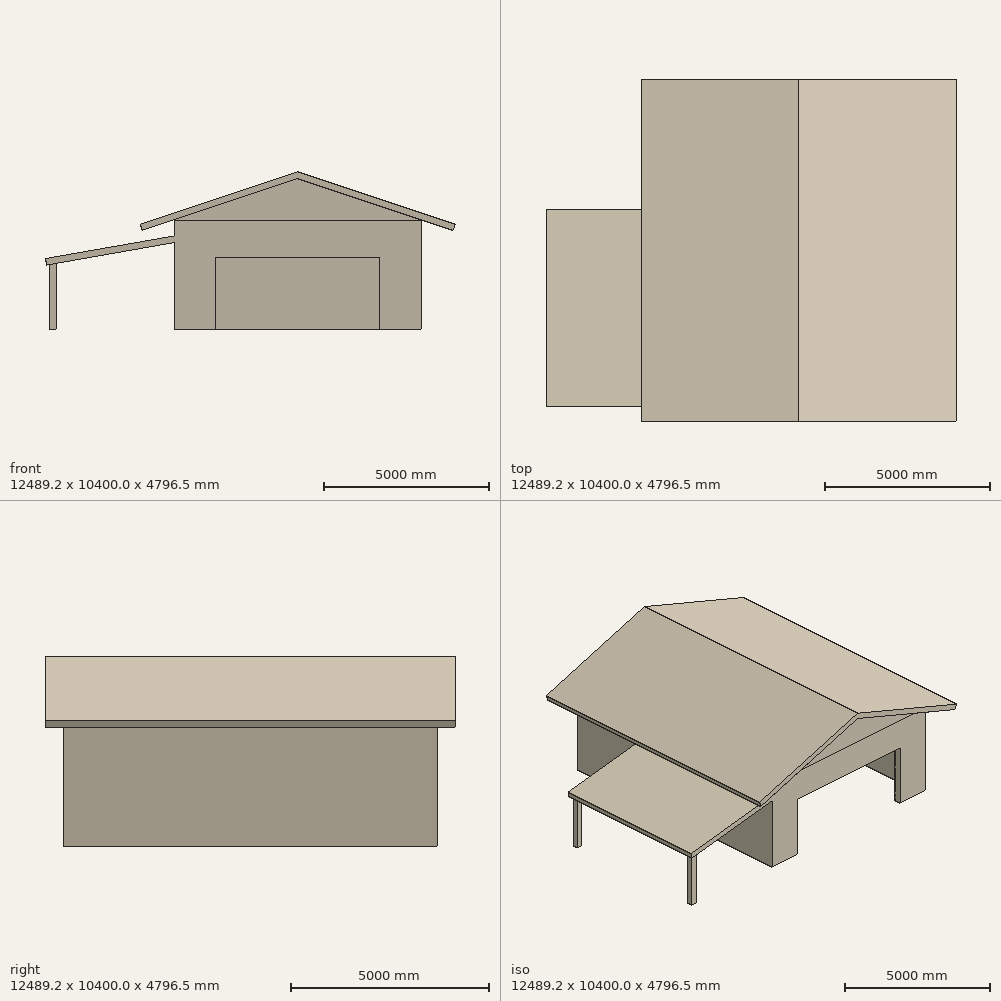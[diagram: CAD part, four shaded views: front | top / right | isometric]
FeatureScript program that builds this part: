
annotation { "Feature Type Name" : "Feature", "Feature Type Description" : "" }
export const myFeature = defineFeature(function(context is Context, id is Id, definition is map)
    precondition{}
    {
        {
            var Q0;
            Q0=qCreatedBy(makeId("Top.planeOp"),FACE);
            var sketch = newSketch(context, id + "F0", { "sketchPlane" : qUnion([Q0])});
            skLineSegment(sketch, "E0.bottom", {"start": v(-7500, 9500) * mm, "end": v(0, 9500) * mm});
            skLineSegment(sketch, "E0.top", {"start": v(-7500, 0) * mm, "end": v(0, 0) * mm});
            skLineSegment(sketch, "E0.left", {"start": v(-7500, 9500) * mm, "end": v(-7500, 0) * mm});
            skLineSegment(sketch, "E0.right", {"start": v(0, 9500) * mm, "end": v(0, 0) * mm});
            skLineSegment(sketch, "E1.bottom", {"start": v(-6186.75, 4848.57) * mm, "end": v(-4436.75, 4848.57) * mm, "construction": true});
            skLineSegment(sketch, "E1.top", {"start": v(-6186.75, 648.57) * mm, "end": v(-4436.75, 648.57) * mm, "construction": true});
            skLineSegment(sketch, "E1.left", {"start": v(-6186.75, 4848.57) * mm, "end": v(-6186.75, 648.57) * mm, "construction": true});
            skLineSegment(sketch, "E1.right", {"start": v(-4436.75, 4848.57) * mm, "end": v(-4436.75, 648.57) * mm, "construction": true});
            skLineSegment(sketch, "E2", {"start": v(0, 7250) * mm, "end": v(-7500, 7250) * mm, "construction": true});
            skSolve(sketch);
        }
        {
            var Q0;
            Q0=makeQuery(id+"F0.imprint","IMPRINT",FACE,{"disambiguationData":[TD([[makeQuery(id+"F0.imprint","IMPRINT",EDGE,{"derivedFrom":sQuery(id+"F0.wireOp",EDGE,"E0.bottom")}),-1.0]])]});
            extrude(context, id + "F1", {"entities" : qUnion([Q0]), "offsetDistance" : 25 * mm, "depth" : 3300 * mm});
        }
        {
            var Q0;
            Q0=makeQuery(id+"F1.opExtrude","SWEPT_FACE",FACE,{"disambiguationData":[OSD([sQuery(id+"F0.wireOp",EDGE,"E0.top")])]});
            var Q1;
            Q1=makeQuery(id+"F1.opExtrude","SWEPT_FACE",FACE,{"disambiguationData":[OSD([sQuery(id+"F0.wireOp",EDGE,"E0.bottom")])]});
            cPlane(context, id + "F2", {"entities" : qUnion([Q0, Q1]), "cplaneType" : CPlaneType.MID_PLANE, "offset" : 25 * mm, "width" : 150 * mm, "height" : 150 * mm});
        }
        {
            var Q0;
            Q0=qCreatedBy(id+"F2.planeOp",FACE);
            var sketch = newSketch(context, id + "F3", { "sketchPlane" : qUnion([Q0])});
            skLineSegment(sketch, "E3", {"start": v(-3750, 3557.53) * mm, "end": v(-3750, 7.87) * mm, "construction": true});
            skLineSegment(sketch, "E4", {"start": v(-3750, 4796.48) * mm, "end": v(-8550, 3196.48) * mm});
            skLineSegment(sketch, "E5", {"start": v(-8550, 3196.48) * mm, "end": v(-8486.75, 3006.75) * mm});
            skLineSegment(sketch, "E6", {"start": v(-8486.75, 3006.75) * mm, "end": v(-3750, 4585.66) * mm});
            skLineSegment(sketch, "E7.MirrorCS", {"start": v(986.75, 3006.75) * mm, "end": v(-3750, 4585.66) * mm});
            skLineSegment(sketch, "E8.MirrorCS", {"start": v(-3750, 4796.48) * mm, "end": v(1050, 3196.48) * mm});
            skLineSegment(sketch, "E9.MirrorCS", {"start": v(1050, 3196.48) * mm, "end": v(986.75, 3006.75) * mm});
            skLineSegment(sketch, "E10", {"start": v(-8550, 3196.48) * mm, "end": v(1050, 3196.48) * mm, "construction": true});
            skSolve(sketch);
        }
        {
            var Q0;
            Q0 = qSketchRegion(id + "F3", true);
            extrude(context, id + "F4", {"entities" : qUnion([Q0]), "depth" : 5200 * mm, "hasSecondDirection" : true, "secondDirectionOppositeDirection" : true, "secondDirectionDepth" : 5200 * mm});
        }
        {
            var Q0;
            Q0=makeQuery(id+"F1.opExtrude","SWEPT_FACE",FACE,{"disambiguationData":[OSD([sQuery(id+"F0.wireOp",EDGE,"E0.top")])]});
            var sketch = newSketch(context, id + "F5", { "sketchPlane" : qUnion([Q0])});
            skLineSegment(sketch, "E11", {"start": v(-3750, 4585.66) * mm, "end": v(-7500, 3335.66) * mm});
            skLineSegment(sketch, "E12", {"start": v(0, 3335.66) * mm, "end": v(-3750, 4585.66) * mm});
            skLineSegment(sketch, "E13", {"start": v(-7500, 3335.66) * mm, "end": v(-7500, 3300) * mm});
            skLineSegment(sketch, "E14", {"start": v(0, 3335.66) * mm, "end": v(0, 3300) * mm});
            skLineSegment(sketch, "E15", {"start": v(-7500, 3300) * mm, "end": v(0, 3300) * mm});
            skSolve(sketch);
        }
        {
            var Q0;
            Q0 = qSketchRegion(id + "F5", true);
            var Q1;
            Q1=makeQuery(id+"F1.opExtrude","SWEPT_FACE",FACE,{"disambiguationData":[OSD([sQuery(id+"F0.wireOp",EDGE,"E0.bottom")])]});
            extrude(context, id + "F6", {"entities" : qUnion([Q0]), "endBound" : BoundingType.UP_TO_SURFACE, "oppositeDirection" : true, "endBoundEntityFace" : qUnion([Q1]), "depth" : 25 * mm});
        }
        {
            var Q0;
            Q0=makeQuery(id+"F1.opExtrude","SWEPT_FACE",FACE,{"disambiguationData":[OSD([sQuery(id+"F0.wireOp",EDGE,"E0.top")])]});
            var sketch = newSketch(context, id + "F7", { "sketchPlane" : qUnion([Q0])});
            skLineSegment(sketch, "E16", {"start": v(-7500, 2844.03) * mm, "end": v(-11439.23, 2149.44) * mm});
            skLineSegment(sketch, "E17", {"start": v(-11439.23, 2149.44) * mm, "end": v(-11404.5, 1952.48) * mm});
            skLineSegment(sketch, "E18", {"start": v(-11404.5, 1952.48) * mm, "end": v(-7500, 2640.95) * mm});
            skLineSegment(sketch, "E19", {"start": v(-7500, 2844.03) * mm, "end": v(-7500, 2640.95) * mm});
            skSolve(sketch);
        }
        {
            var Q0;
            Q0 = qSketchRegion(id + "F7", true);
            extrude(context, id + "F8", {"entities" : qUnion([Q0]), "operationType" : NewBodyOperationType.ADD, "oppositeDirection" : true, "depth" : 6000 * mm});
        }
        {
            var Q0;
            Q0=makeQuery(id+"F0.imprint","IMPRINT",FACE,{"disambiguationData":[TD([[makeQuery(id+"F0.imprint","IMPRINT",EDGE,{"derivedFrom":sQuery(id+"F0.wireOp",EDGE,"E0.bottom")}),-1.0]])]});
            var sketch = newSketch(context, id + "F9", { "sketchPlane" : qUnion([Q0])});
            skLineSegment(sketch, "E20.bottom", {"start": v(-11104.5, 100) * mm, "end": v(-11304.5, 100) * mm});
            skLineSegment(sketch, "E20.top", {"start": v(-11104.5, 300) * mm, "end": v(-11304.5, 300) * mm});
            skLineSegment(sketch, "E20.left", {"start": v(-11104.5, 100) * mm, "end": v(-11104.5, 300) * mm});
            skLineSegment(sketch, "E20.right", {"start": v(-11304.5, 100) * mm, "end": v(-11304.5, 300) * mm});
            skLineSegment(sketch, "E21.bottom", {"start": v(-11304.5, 5900) * mm, "end": v(-11104.5, 5900) * mm});
            skLineSegment(sketch, "E21.top", {"start": v(-11304.5, 5700) * mm, "end": v(-11104.5, 5700) * mm});
            skLineSegment(sketch, "E21.left", {"start": v(-11304.5, 5900) * mm, "end": v(-11304.5, 5700) * mm});
            skLineSegment(sketch, "E21.right", {"start": v(-11104.5, 5900) * mm, "end": v(-11104.5, 5700) * mm});
            skSolve(sketch);
        }
        {
            var Q0;
            Q0 = qSketchRegion(id + "F9", true);
            extrude(context, id + "F10", {"entities" : qUnion([Q0]), "operationType" : NewBodyOperationType.ADD, "depth" : 2150 * mm});
        }
        {
            var Q0;
            Q0=makeQuery(id+"F0.imprint","IMPRINT",FACE,{"disambiguationData":[TD([[makeQuery(id+"F0.imprint","IMPRINT",EDGE,{"derivedFrom":sQuery(id+"F0.wireOp",EDGE,"E0.bottom")}),-1.0]])]});
            var sketch = newSketch(context, id + "F11", { "sketchPlane" : qUnion([Q0])});
            skLineSegment(sketch, "E22.bottom", {"start": v(-7250, 250) * mm, "end": v(-250, 250) * mm});
            skLineSegment(sketch, "E22.top", {"start": v(-7250, 9250) * mm, "end": v(-250, 9250) * mm});
            skLineSegment(sketch, "E22.left", {"start": v(-7250, 250) * mm, "end": v(-7250, 9250) * mm});
            skLineSegment(sketch, "E22.right", {"start": v(-250, 250) * mm, "end": v(-250, 9250) * mm});
            skSolve(sketch);
        }
        {
            var Q0;
            Q0 = qSketchRegion(id + "F11", true);
            extrude(context, id + "F12", {"entities" : qUnion([Q0]), "operationType" : NewBodyOperationType.REMOVE, "depth" : 2800 * mm});
        }
        {
            var Q0;
            Q0=makeQuery(id+"F8.boolean.opBoolean","MERGE",FACE,{"derivedFrom":[makeQuery(id+"F1.opExtrude","SWEPT_FACE",FACE,{"disambiguationData":[OSD([sQuery(id+"F0.wireOp",EDGE,"E0.top")])]}),makeQuery(id+"F8.opExtrude","CAP_FACE",FACE,{"disambiguationData":[OSD([sQuery(id+"F7.wireOp",EDGE,"E16"),sQuery(id+"F7.wireOp",EDGE,"E17"),sQuery(id+"F7.wireOp",EDGE,"E18"),sQuery(id+"F7.wireOp",EDGE,"E19")])],"isStart":true})]});
            var sketch = newSketch(context, id + "F13", { "sketchPlane" : qUnion([Q0])});
            skLineSegment(sketch, "E23.bottom", {"start": v(-6250, 0) * mm, "end": v(-1250, 0) * mm});
            skLineSegment(sketch, "E23.top", {"start": v(-6250, 2200) * mm, "end": v(-1250, 2200) * mm});
            skLineSegment(sketch, "E23.left", {"start": v(-6250, 0) * mm, "end": v(-6250, 2200) * mm});
            skLineSegment(sketch, "E23.right", {"start": v(-1250, 0) * mm, "end": v(-1250, 2200) * mm});
            skLineSegment(sketch, "E24", {"start": v(-3750, 4957.64) * mm, "end": v(-3750, -1395.58) * mm, "construction": true});
            skSolve(sketch);
        }
        {
            var Q0;
            Q0 = qSketchRegion(id + "F13", true);
            extrude(context, id + "F14", {"entities" : qUnion([Q0]), "operationType" : NewBodyOperationType.REMOVE, "endBound" : BoundingType.UP_TO_NEXT, "oppositeDirection" : true, "depth" : 25 * mm});
        }
    });
